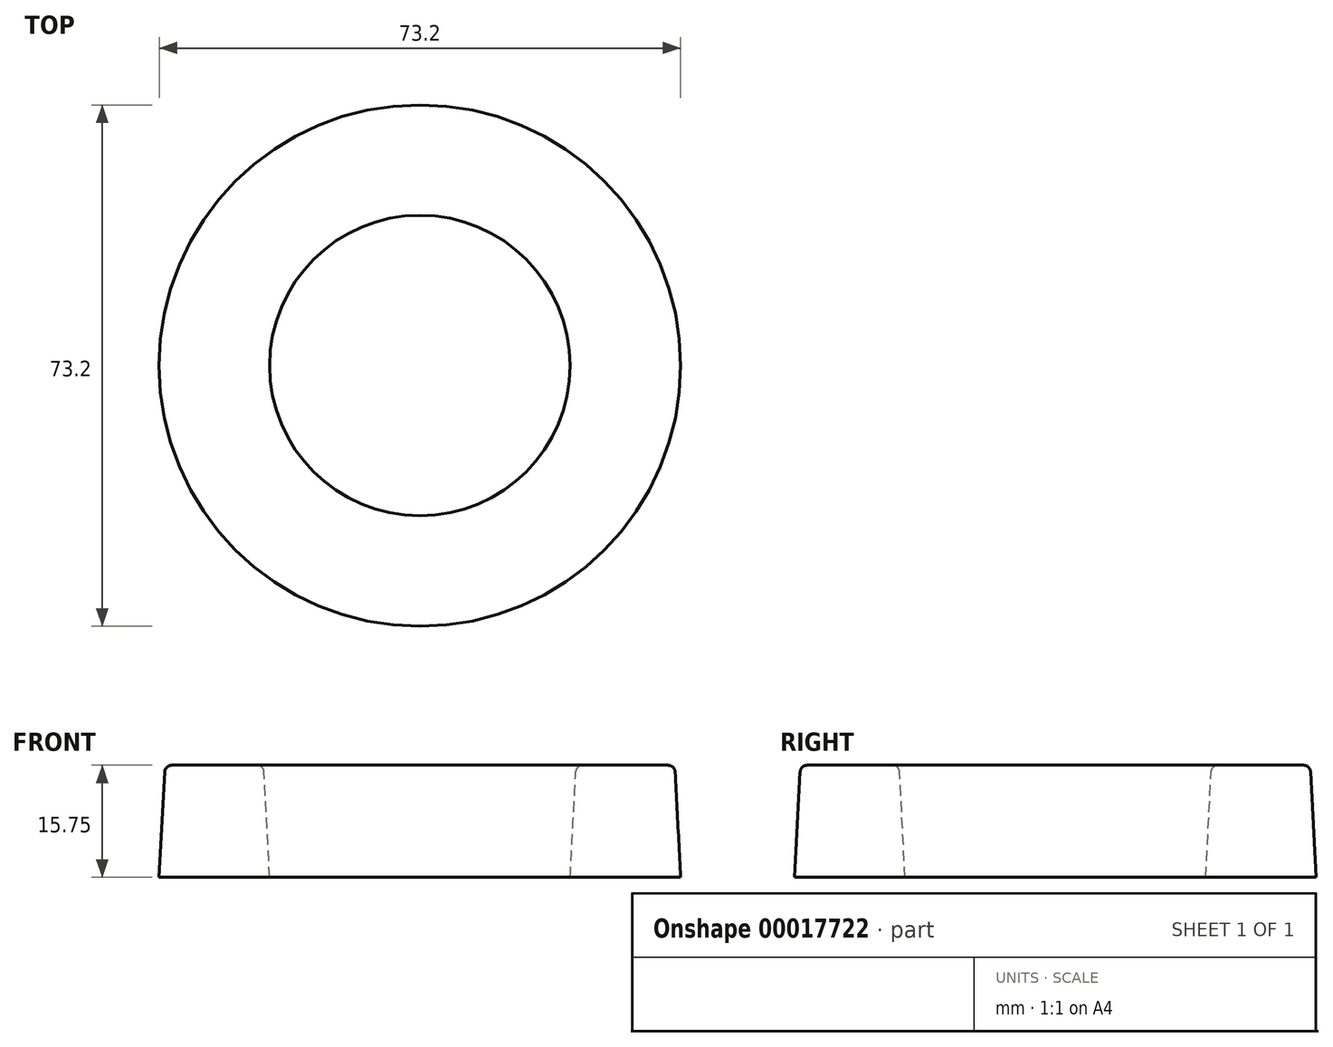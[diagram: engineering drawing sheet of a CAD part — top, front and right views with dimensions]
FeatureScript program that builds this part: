
annotation { "Feature Type Name" : "Feature", "Feature Type Description" : "" }
export const myFeature = defineFeature(function(context is Context, id is Id, definition is map)
    precondition{}
    {
        {
            var Q0;
            Q0=qCreatedBy(makeId("Front.planeOp"),FACE);
            var sketch = newSketch(context, id + "F0", { "sketchPlane" : qUnion([Q0])});
            skLineSegment(sketch, "E0", {"start": v(-21.1, 0) * mm, "end": v(-21.87, 14.8) * mm});
            skLineSegment(sketch, "E1", {"start": v(-22.86, 15.75) * mm, "end": v(-34.84, 15.75) * mm});
            skLineSegment(sketch, "E2", {"start": v(-35.83, 14.8) * mm, "end": v(-36.6, 0) * mm});
            skLineSegment(sketch, "E3", {"start": v(-36.6, 0) * mm, "end": v(-21.1, 0) * mm});
            skLineSegment(sketch, "E4", {"start": v(0, 39.86) * mm, "end": v(0, -45.62) * mm, "construction": true});
            skPoint(sketch, "E5.visualSharp", {"position": v(-35.78, 15.75) * mm});
            skArc(sketch, "E5.filletArc", {"start": v(-34.84, 15.75) * mm, "mid": v(-35.52, 15.48) * mm, "end": v(-35.83, 14.8) * mm});
            skPoint(sketch, "E6.visualSharp", {"position": v(-21.92, 15.75) * mm});
            skArc(sketch, "E6.filletArc", {"start": v(-21.87, 14.8) * mm, "mid": v(-22.18, 15.48) * mm, "end": v(-22.86, 15.75) * mm});
            skSolve(sketch);
        }
        {
            var Q0;
            Q0=makeQuery(id+"F0.imprint","IMPRINT",FACE,{"disambiguationData":[TD([[makeQuery(id+"F0.imprint","IMPRINT",EDGE,{"derivedFrom":sQuery(id+"F0.wireOp",EDGE,"E0")}),1.0]])]});
            var Q1;
            Q1=sQuery(id+"F0.wireOp",EDGE,"E4");
            revolve(context, id + "F1", {"entities" : qUnion([Q0]), "axis" : qUnion([Q1]), "revolveType" : RevolveType.FULL});
        }
    });
